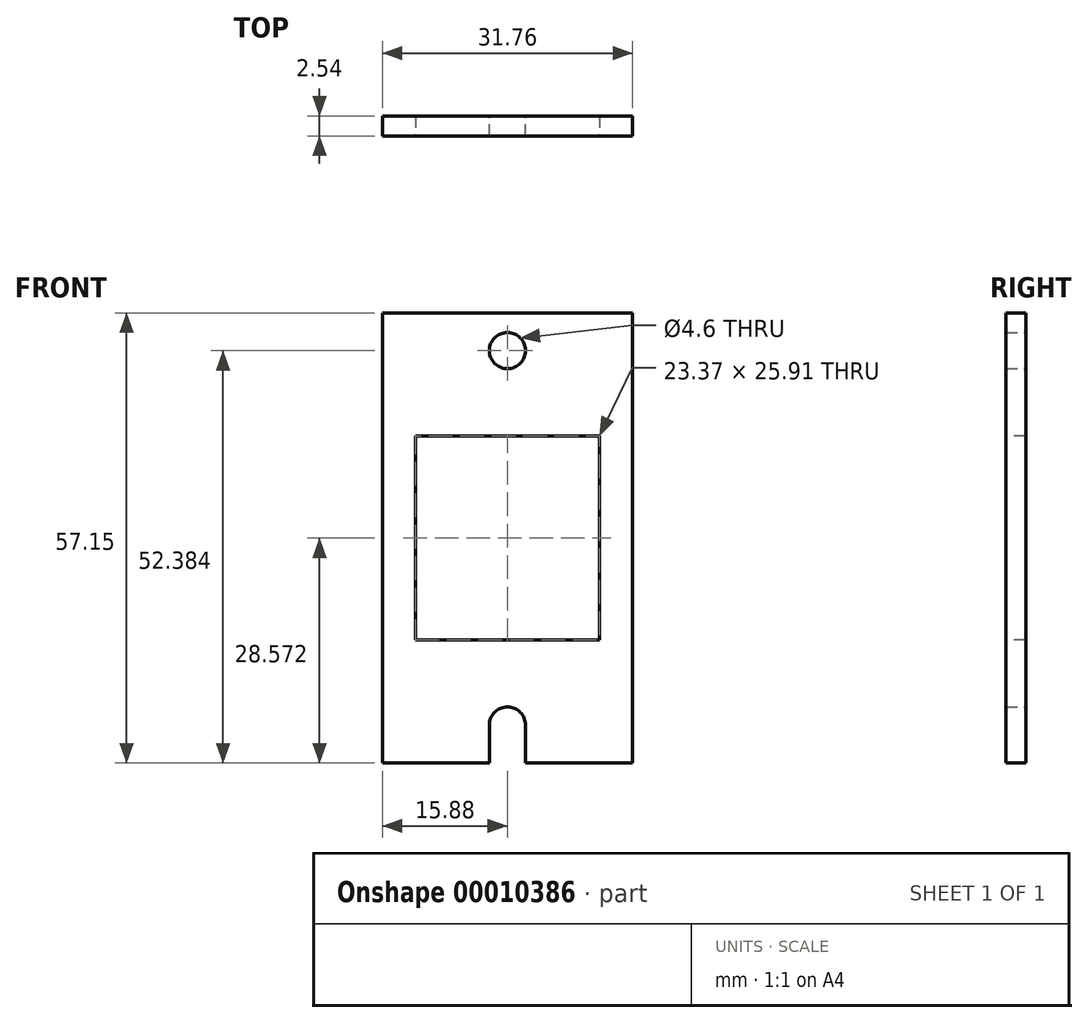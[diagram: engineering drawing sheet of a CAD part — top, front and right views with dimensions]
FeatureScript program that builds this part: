
annotation { "Feature Type Name" : "Feature", "Feature Type Description" : "" }
export const myFeature = defineFeature(function(context is Context, id is Id, definition is map)
    precondition{}
    {
        {
            var Q0;
            Q0=qCreatedBy(makeId("Front.planeOp"),FACE);
            var sketch = newSketch(context, id + "F0", { "sketchPlane" : qUnion([Q0])});
            skLineSegment(sketch, "E0.bottom", {"start": v(-15.87, 37.4) * mm, "end": v(15.88, 37.4) * mm});
            skLineSegment(sketch, "E0.top", {"start": v(-15.87, -19.75) * mm, "end": v(-2.3, -19.75) * mm});
            skLineSegment(sketch, "E0.left", {"start": v(-15.87, 37.4) * mm, "end": v(-15.87, -19.75) * mm});
            skLineSegment(sketch, "E0.right", {"start": v(15.88, 37.4) * mm, "end": v(15.88, -19.75) * mm});
            skCircle(sketch, "E1", {"center": v(0, 32.63) * mm, "radius": 2.3 * mm});
            skArc(sketch, "E2", {"start": v(2.3, -14.94) * mm, "mid": v(0, -12.64) * mm, "end": v(-2.3, -14.94) * mm});
            skLineSegment(sketch, "E3", {"start": v(-2.3, -14.94) * mm, "end": v(-2.3, -19.75) * mm});
            skLineSegment(sketch, "E4", {"start": v(2.3, -14.94) * mm, "end": v(2.3, -19.75) * mm});
            skLineSegment(sketch, "E5.trimOffspring", {"start": v(2.3, -19.75) * mm, "end": v(15.88, -19.75) * mm});
            skSolve(sketch);
        }
        {
            var Q0;
            Q0 = qSketchRegion(id + "F0", true);
            extrude(context, id + "F1", {"entities" : qUnion([Q0]), "depth" : 2.54 * mm});
        }
        {
            var Q0;
            Q0=makeQuery(id+"F1.opExtrude","CAP_FACE",FACE,{"disambiguationData":[OSD([sQuery(id+"F0.wireOp",EDGE,"E0.bottom"),sQuery(id+"F0.wireOp",EDGE,"E0.top"),sQuery(id+"F0.wireOp",EDGE,"E0.left"),sQuery(id+"F0.wireOp",EDGE,"E0.right"),sQuery(id+"F0.wireOp",EDGE,"E1"),sQuery(id+"F0.wireOp",EDGE,"E2"),sQuery(id+"F0.wireOp",EDGE,"E3"),sQuery(id+"F0.wireOp",EDGE,"E4"),sQuery(id+"F0.wireOp",EDGE,"E5.trimOffspring")])],"isStart":false});
            var sketch = newSketch(context, id + "F2", { "sketchPlane" : qUnion([Q0])});
            skLineSegment(sketch, "E6.bottom", {"start": v(-11.68, 21.78) * mm, "end": v(11.68, 21.78) * mm});
            skLineSegment(sketch, "E6.top", {"start": v(-11.68, -4.13) * mm, "end": v(11.68, -4.13) * mm});
            skLineSegment(sketch, "E6.left", {"start": v(-11.68, 21.78) * mm, "end": v(-11.68, -4.13) * mm});
            skLineSegment(sketch, "E6.right", {"start": v(11.68, 21.78) * mm, "end": v(11.68, -4.13) * mm});
            skSolve(sketch);
        }
        {
            var Q0;
            Q0 = qSketchRegion(id + "F2", true);
            extrude(context, id + "F3", {"entities" : qUnion([Q0]), "operationType" : NewBodyOperationType.REMOVE, "oppositeDirection" : true, "depth" : 25.4 * mm});
        }
    });
